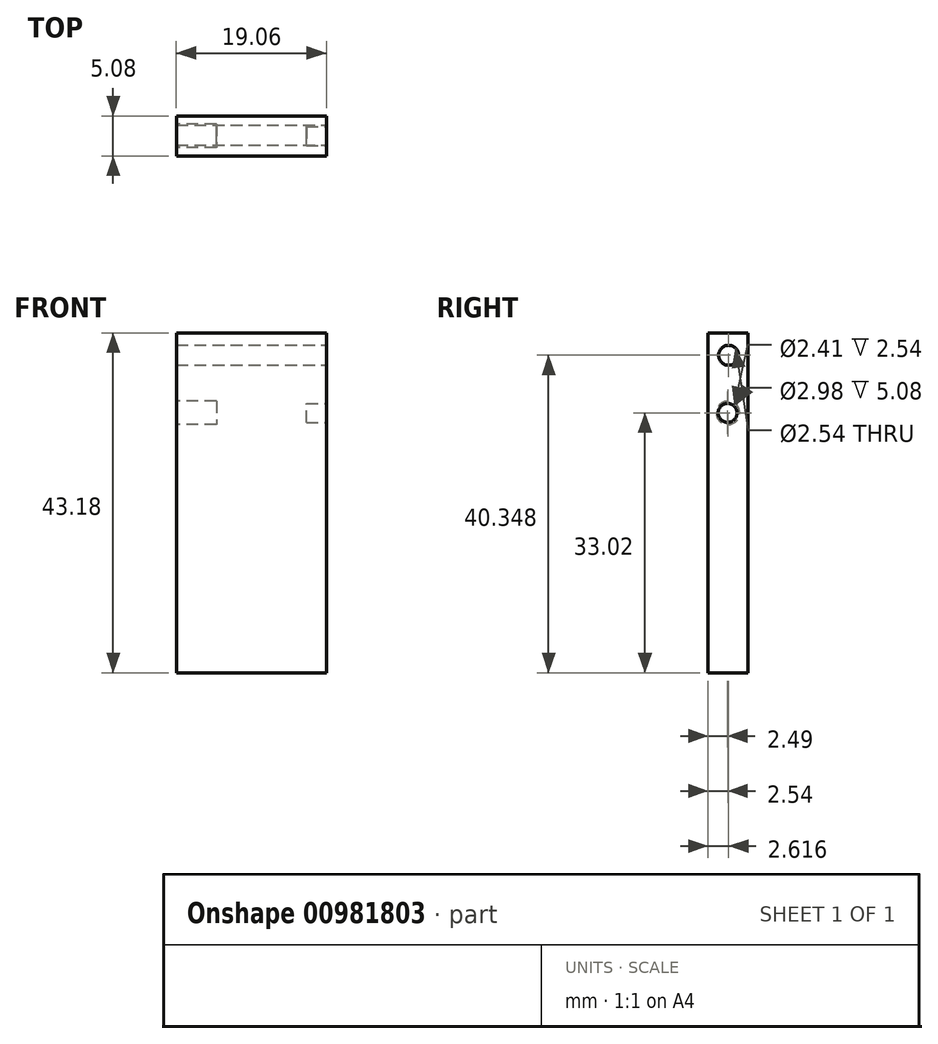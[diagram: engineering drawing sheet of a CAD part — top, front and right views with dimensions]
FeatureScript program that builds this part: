
annotation { "Feature Type Name" : "Feature", "Feature Type Description" : "" }
export const myFeature = defineFeature(function(context is Context, id is Id, definition is map)
    precondition{}
    {
        {
            var Q0;
            Q0=qCreatedBy(makeId("Front.planeOp"),FACE);
            var sketch = newSketch(context, id + "F0", { "sketchPlane" : qUnion([Q0])});
            skLineSegment(sketch, "E0.bottom", {"start": v(9.53, 21.59) * mm, "end": v(-9.52, 21.59) * mm});
            skLineSegment(sketch, "E0.top", {"start": v(9.53, -21.59) * mm, "end": v(-9.53, -21.59) * mm});
            skLineSegment(sketch, "E0.left", {"start": v(9.53, 21.59) * mm, "end": v(9.53, -21.59) * mm});
            skLineSegment(sketch, "E0.right", {"start": v(-9.52, 21.59) * mm, "end": v(-9.53, -21.59) * mm});
            skPoint(sketch, "E0.middle", {"position": v(0, 0) * mm});
            skSolve(sketch);
        }
        {
            var Q0;
            Q0=makeQuery(id+"F0.imprint","IMPRINT",FACE,{"disambiguationData":[TD([[makeQuery(id+"F0.imprint","IMPRINT",EDGE,{"derivedFrom":sQuery(id+"F0.wireOp",EDGE,"E0.bottom")}),1.0]])]});
            extrude(context, id + "F1", {"entities" : qUnion([Q0]), "depth" : 5.08 * mm, "offsetDistance" : 25.4 * mm});
        }
        {
            var Q0;
            Q0=makeQuery(id+"F1.opExtrude","SWEPT_FACE",FACE,{"disambiguationData":[OSD([sQuery(id+"F0.wireOp",EDGE,"E0.left")])]});
            var sketch = newSketch(context, id + "F2", { "sketchPlane" : qUnion([Q0])});
            skCircle(sketch, "E1", {"center": v(-2.6, 11.43) * mm, "radius": 1.2 * mm});
            skSolve(sketch);
        }
        {
            var Q0;
            Q0=makeQuery(id+"F2.imprint","IMPRINT",FACE,{"disambiguationData":[TD([[makeQuery(id+"F2.imprint","IMPRINT",EDGE,{"derivedFrom":sQuery(id+"F2.wireOp",EDGE,"E1")}),1.0]])]});
            extrude(context, id + "F3", {"entities" : qUnion([Q0]), "operationType" : NewBodyOperationType.REMOVE, "oppositeDirection" : true, "depth" : 2.54 * mm, "offsetDistance" : 25.4 * mm});
        }
        {
            var Q0;
            Q0=makeQuery(id+"F1.opExtrude","SWEPT_FACE",FACE,{"disambiguationData":[OSD([sQuery(id+"F0.wireOp",EDGE,"E0.right")])]});
            var sketch = newSketch(context, id + "F4", { "sketchPlane" : qUnion([Q0])});
            skCircle(sketch, "E2", {"center": v(2.54, 11.43) * mm, "radius": 1.49 * mm});
            skPoint(sketch, "E2.centerSnap0", {"position": v(2.54, 21.59) * mm});
            skSolve(sketch);
        }
        {
            var Q0;
            Q0=makeQuery(id+"F4.imprint","IMPRINT",FACE,{"disambiguationData":[TD([[makeQuery(id+"F4.imprint","IMPRINT",EDGE,{"derivedFrom":sQuery(id+"F4.wireOp",EDGE,"E2")}),1.0]])]});
            extrude(context, id + "F5", {"entities" : qUnion([Q0]), "operationType" : NewBodyOperationType.REMOVE, "oppositeDirection" : true, "depth" : 5.08 * mm, "offsetDistance" : 25.4 * mm});
        }
        {
            var Q0;
            Q0=makeQuery(id+"F1.opExtrude","SWEPT_FACE",FACE,{"disambiguationData":[OSD([sQuery(id+"F0.wireOp",EDGE,"E0.left")])]});
            var sketch = newSketch(context, id + "F6", { "sketchPlane" : qUnion([Q0])});
            skCircle(sketch, "E3", {"center": v(-2.46, 18.76) * mm, "radius": 1.27 * mm});
            skSolve(sketch);
        }
        {
            var Q0;
            Q0=makeQuery(id+"F6.imprint","IMPRINT",FACE,{"disambiguationData":[TD([[makeQuery(id+"F6.imprint","IMPRINT",EDGE,{"derivedFrom":sQuery(id+"F6.wireOp",EDGE,"E3")}),1.0]])]});
            extrude(context, id + "F7", {"entities" : qUnion([Q0]), "operationType" : NewBodyOperationType.REMOVE, "oppositeDirection" : true, "depth" : 25.4 * mm, "offsetDistance" : 25.4 * mm});
        }
    });
